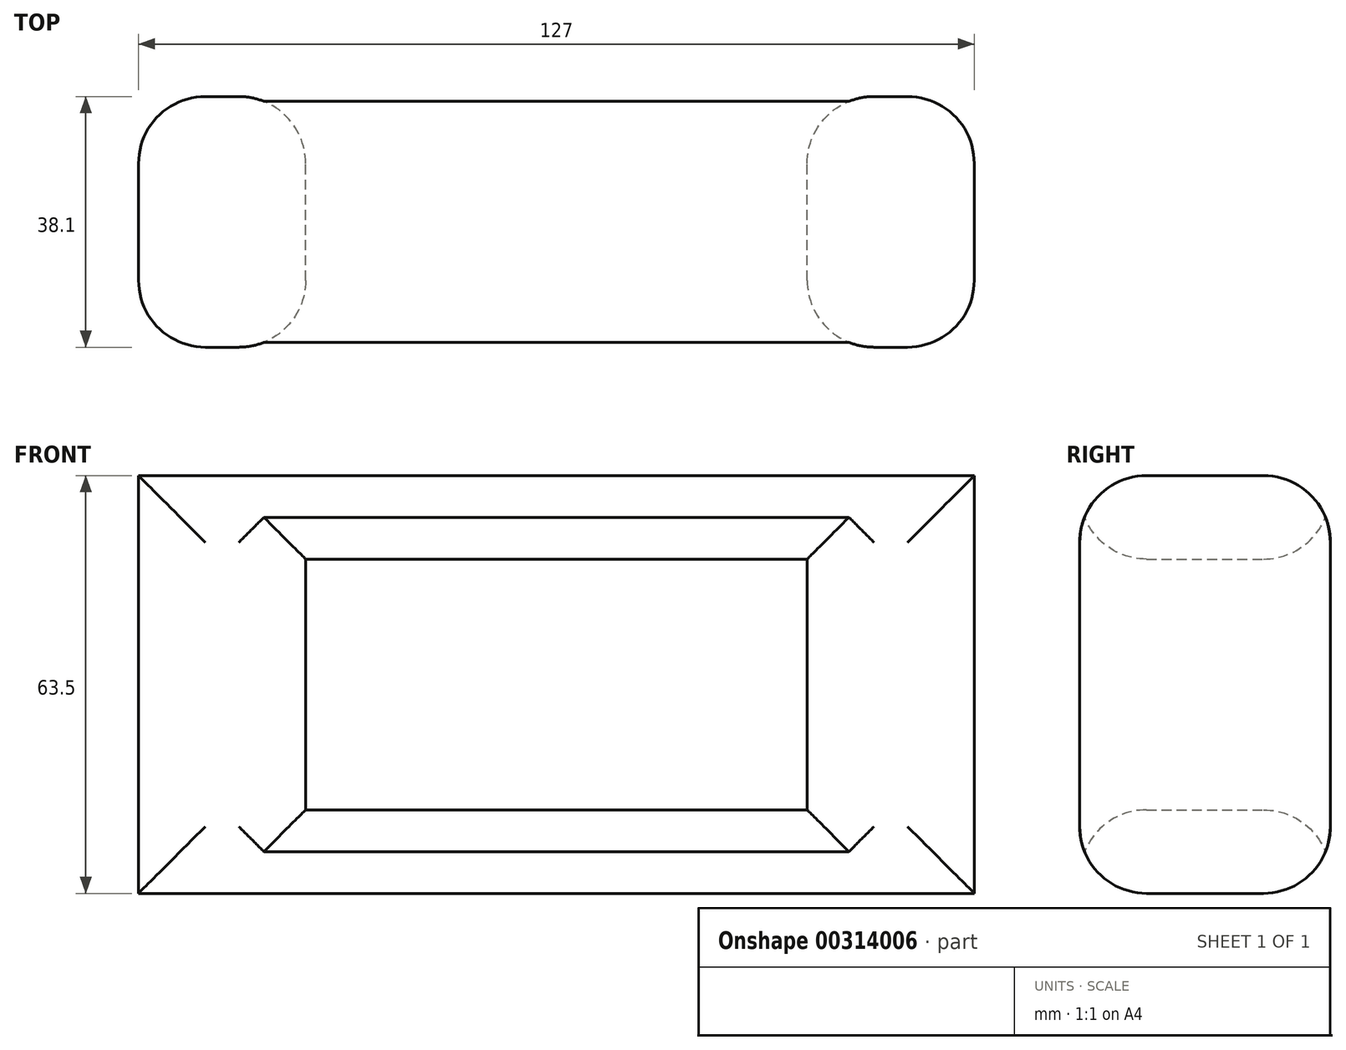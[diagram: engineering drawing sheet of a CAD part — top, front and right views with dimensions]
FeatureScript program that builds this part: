
annotation { "Feature Type Name" : "Feature", "Feature Type Description" : "" }
export const myFeature = defineFeature(function(context is Context, id is Id, definition is map)
    precondition{}
    {
        {
            var Q0;
            Q0=qCreatedBy(makeId("Front.planeOp"),FACE);
            var sketch = newSketch(context, id + "F0", { "sketchPlane" : qUnion([Q0])});
            skLineSegment(sketch, "E0.bottom", {"start": v(63.5, -31.75) * mm, "end": v(-63.5, -31.75) * mm});
            skLineSegment(sketch, "E0.top", {"start": v(63.5, 31.75) * mm, "end": v(-63.5, 31.75) * mm});
            skLineSegment(sketch, "E0.left", {"start": v(63.5, -31.75) * mm, "end": v(63.5, 31.75) * mm});
            skLineSegment(sketch, "E0.right", {"start": v(-63.5, -31.75) * mm, "end": v(-63.5, 31.75) * mm});
            skPoint(sketch, "E0.middle", {"position": v(0, 0) * mm});
            skLineSegment(sketch, "E1.bottom", {"start": v(-38.1, -19.05) * mm, "end": v(38.1, -19.05) * mm});
            skLineSegment(sketch, "E1.top", {"start": v(-38.1, 19.05) * mm, "end": v(38.1, 19.05) * mm});
            skLineSegment(sketch, "E1.left", {"start": v(-38.1, -19.05) * mm, "end": v(-38.1, 19.05) * mm});
            skLineSegment(sketch, "E1.right", {"start": v(38.1, -19.05) * mm, "end": v(38.1, 19.05) * mm});
            skSolve(sketch);
        }
        {
            var Q0;
            Q0 = qSketchRegion(id + "F0", true);
            extrude(context, id + "F1", {"entities" : qUnion([Q0]), "depth" : 38.1 * mm});
        }
        {
            var Q0;
            Q0=makeQuery(id+"F1.opExtrude","CAP_FACE",FACE,{"disambiguationData":[OSD([sQuery(id+"F0.wireOp",EDGE,"E0.bottom"),sQuery(id+"F0.wireOp",EDGE,"E0.top"),sQuery(id+"F0.wireOp",EDGE,"E0.left"),sQuery(id+"F0.wireOp",EDGE,"E0.right"),sQuery(id+"F0.wireOp",EDGE,"E1.bottom"),sQuery(id+"F0.wireOp",EDGE,"E1.top"),sQuery(id+"F0.wireOp",EDGE,"E1.left"),sQuery(id+"F0.wireOp",EDGE,"E1.right")])],"isStart":false});
            var Q1;
            Q1=makeQuery(id+"F1.opExtrude","CAP_FACE",FACE,{"disambiguationData":[OSD([sQuery(id+"F0.wireOp",EDGE,"E0.bottom"),sQuery(id+"F0.wireOp",EDGE,"E0.top"),sQuery(id+"F0.wireOp",EDGE,"E0.left"),sQuery(id+"F0.wireOp",EDGE,"E0.right"),sQuery(id+"F0.wireOp",EDGE,"E1.bottom"),sQuery(id+"F0.wireOp",EDGE,"E1.top"),sQuery(id+"F0.wireOp",EDGE,"E1.left"),sQuery(id+"F0.wireOp",EDGE,"E1.right")])],"isStart":true});
            fillet(context, id + "F2", {"entities" : qUnion([Q0, Q1]), "radius" : 10.16 * mm, "tangentPropagation" : true, "allowEdgeOverflow" : false});
        }
    });
